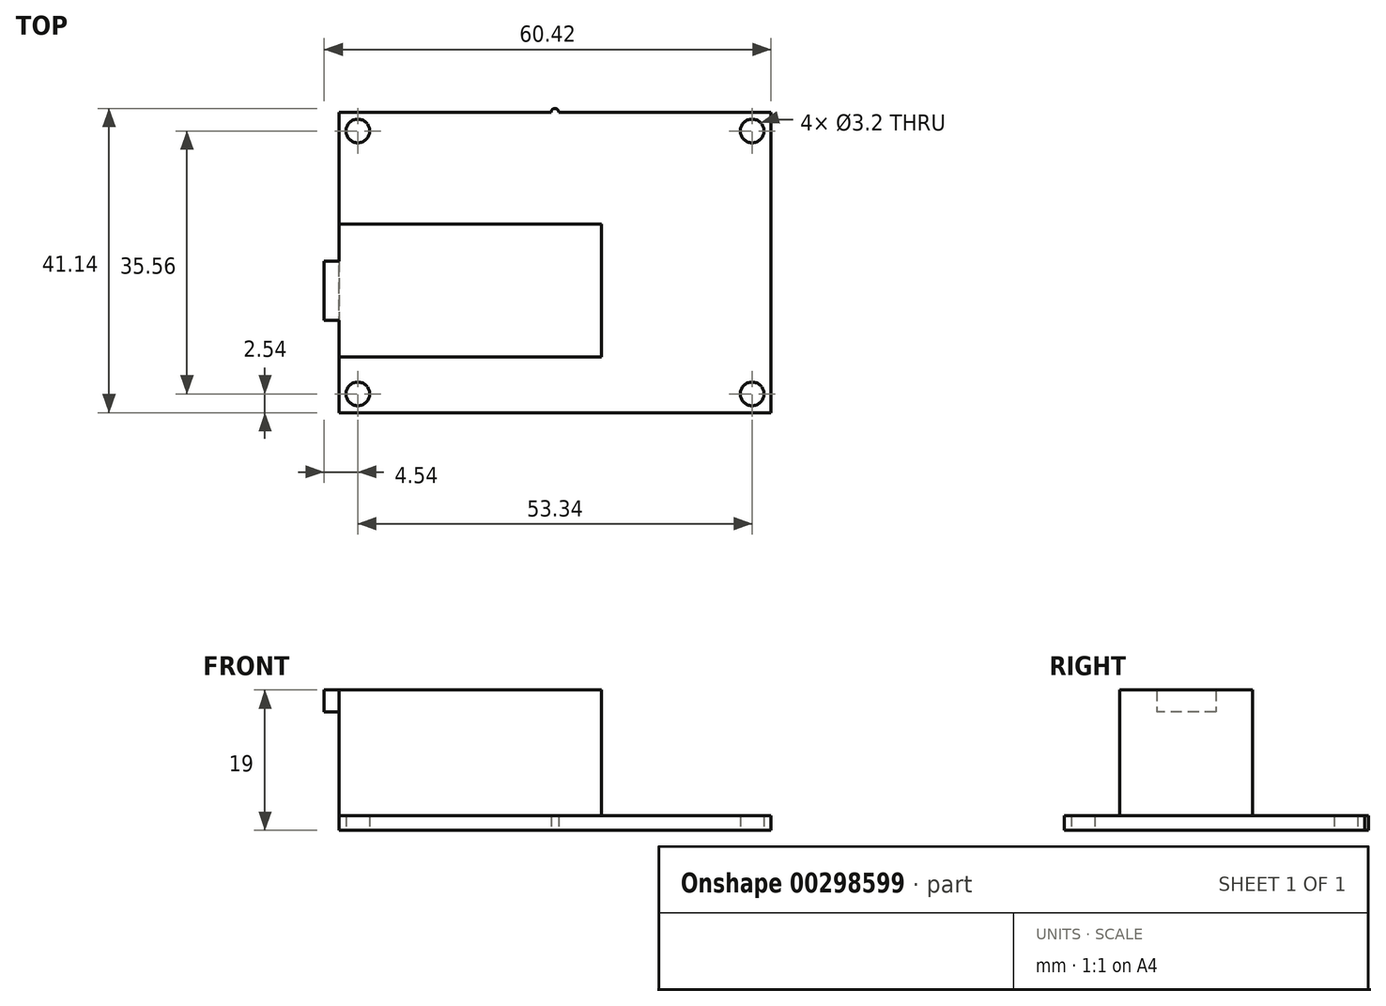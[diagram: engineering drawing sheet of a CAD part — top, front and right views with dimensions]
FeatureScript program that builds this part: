
annotation { "Feature Type Name" : "Feature", "Feature Type Description" : "" }
export const myFeature = defineFeature(function(context is Context, id is Id, definition is map)
    precondition{}
    {
        {
            var Q0;
            Q0=qCreatedBy(makeId("Top.planeOp"),FACE);
            var sketch = newSketch(context, id + "F0", { "sketchPlane" : qUnion([Q0])});
            skLineSegment(sketch, "E0.bottom", {"start": v(29.21, -20.32) * mm, "end": v(-29.21, -20.32) * mm});
            skLineSegment(sketch, "E0.top", {"start": v(29.21, 20.32) * mm, "end": v(-29.21, 20.32) * mm});
            skLineSegment(sketch, "E0.left", {"start": v(29.21, -20.32) * mm, "end": v(29.21, 20.32) * mm});
            skLineSegment(sketch, "E0.right", {"start": v(-29.21, -20.32) * mm, "end": v(-29.21, 20.32) * mm});
            skPoint(sketch, "E0.middle", {"position": v(0, 0) * mm});
            skCircle(sketch, "E1", {"center": v(-26.67, 17.78) * mm, "radius": 1.6 * mm});
            skCircle(sketch, "E2", {"center": v(26.67, 17.78) * mm, "radius": 1.6 * mm});
            skCircle(sketch, "E3", {"center": v(-26.67, -17.78) * mm, "radius": 1.6 * mm});
            skCircle(sketch, "E4", {"center": v(26.67, -17.78) * mm, "radius": 1.6 * mm});
            skCircle(sketch, "E5", {"center": v(0, 20.32) * mm, "radius": 0.5 * mm});
            skSolve(sketch);
        }
        {
            var Q0;
            Q0 = qSketchRegion(id + "F0", true);
            extrude(context, id + "F1", {"entities" : qUnion([Q0]), "depth" : 2 * mm});
        }
        {
            var Q0;
            Q0=makeQuery(id+"F1.opExtrude","CAP_FACE",FACE,{"disambiguationData":[OSD([sQuery(id+"F0.wireOp",EDGE,"E0.bottom"),sQuery(id+"F0.wireOp",EDGE,"E0.top"),sQuery(id+"F0.wireOp",EDGE,"E0.left"),sQuery(id+"F0.wireOp",EDGE,"E0.right"),sQuery(id+"F0.wireOp",EDGE,"E1"),sQuery(id+"F0.wireOp",EDGE,"E2"),sQuery(id+"F0.wireOp",EDGE,"E3"),sQuery(id+"F0.wireOp",EDGE,"E4"),sQuery(id+"F0.wireOp",EDGE,"E5")])],"isStart":false});
            cPlane(context, id + "F2", {"entities" : qUnion([Q0]), "cplaneType" : CPlaneType.OFFSET, "offset" : 0 * mm, "width" : 150 * mm, "height" : 150 * mm});
        }
        {
            var Q0;
            Q0=qCreatedBy(id+"F2.planeOp",FACE);
            var sketch = newSketch(context, id + "F3", { "sketchPlane" : qUnion([Q0])});
            skLineSegment(sketch, "E6.0", {"start": v(-0.5, 20.32) * mm, "end": v(-29.21, 20.32) * mm, "construction": true});
            skLineSegment(sketch, "E7.0", {"start": v(29.21, -20.32) * mm, "end": v(-29.21, -20.32) * mm, "construction": true});
            skLineSegment(sketch, "E8.0", {"start": v(-29.21, -20.32) * mm, "end": v(-29.21, 20.32) * mm, "construction": true});
            skLineSegment(sketch, "E9", {"start": v(-28.36, 20.32) * mm, "end": v(-28.36, -3.8) * mm, "construction": true});
            skLineSegment(sketch, "E10.bottom", {"start": v(-29.21, 5.2) * mm, "end": v(6.3, 5.2) * mm});
            skLineSegment(sketch, "E10.top", {"start": v(-29.21, -12.8) * mm, "end": v(6.3, -12.8) * mm});
            skLineSegment(sketch, "E10.left", {"start": v(-29.21, 5.2) * mm, "end": v(-29.21, -12.8) * mm});
            skLineSegment(sketch, "E10.right", {"start": v(6.3, 5.2) * mm, "end": v(6.3, -12.8) * mm});
            skLineSegment(sketch, "E11", {"start": v(-28.36, -3.8) * mm, "end": v(-14.28, -3.8) * mm, "construction": true});
            skSolve(sketch);
        }
        {
            var Q0;
            Q0 = qSketchRegion(id + "F3", true);
            extrude(context, id + "F4", {"entities" : qUnion([Q0]), "operationType" : NewBodyOperationType.ADD, "depth" : 17 * mm});
        }
        {
            var Q0;
            Q0=makeQuery(id+"F4.boolean.opBoolean","MERGE",FACE,{"derivedFrom":[makeQuery(id+"F1.opExtrude","SWEPT_FACE",FACE,{"disambiguationData":[OSD([sQuery(id+"F0.wireOp",EDGE,"E0.right")])]}),makeQuery(id+"F4.opExtrude","SWEPT_FACE",FACE,{"disambiguationData":[OSD([sQuery(id+"F3.wireOp",EDGE,"E10.left")])]})]});
            cPlane(context, id + "F5", {"entities" : qUnion([Q0]), "cplaneType" : CPlaneType.OFFSET, "offset" : 0 * mm, "width" : 150 * mm, "height" : 150 * mm});
        }
        {
            var Q0;
            Q0=qCreatedBy(id+"F5.planeOp",FACE);
            var sketch = newSketch(context, id + "F6", { "sketchPlane" : qUnion([Q0])});
            skLineSegment(sketch, "E12.0", {"start": v(-5.2, 19) * mm, "end": v(12.8, 19) * mm, "construction": true});
            skLineSegment(sketch, "E13.0", {"start": v(-5.2, 19) * mm, "end": v(-5.2, 2) * mm, "construction": true});
            skLineSegment(sketch, "E14.0", {"start": v(12.8, 19) * mm, "end": v(12.8, 2) * mm, "construction": true});
            skLineSegment(sketch, "E15", {"start": v(3.8, 19) * mm, "end": v(3.8, 12) * mm, "construction": true});
            skLineSegment(sketch, "E16.bottom", {"start": v(-0.2, 19) * mm, "end": v(7.81, 19) * mm});
            skLineSegment(sketch, "E16.top", {"start": v(-0.2, 16) * mm, "end": v(7.8, 16) * mm});
            skLineSegment(sketch, "E16.left", {"start": v(-0.2, 19) * mm, "end": v(-0.2, 16) * mm});
            skLineSegment(sketch, "E16.right", {"start": v(7.81, 19) * mm, "end": v(7.81, 16) * mm});
            skSolve(sketch);
        }
        {
            var Q0;
            Q0 = qSketchRegion(id + "F6", true);
            extrude(context, id + "F7", {"entities" : qUnion([Q0]), "operationType" : NewBodyOperationType.ADD, "depth" : 2 * mm});
        }
    });
